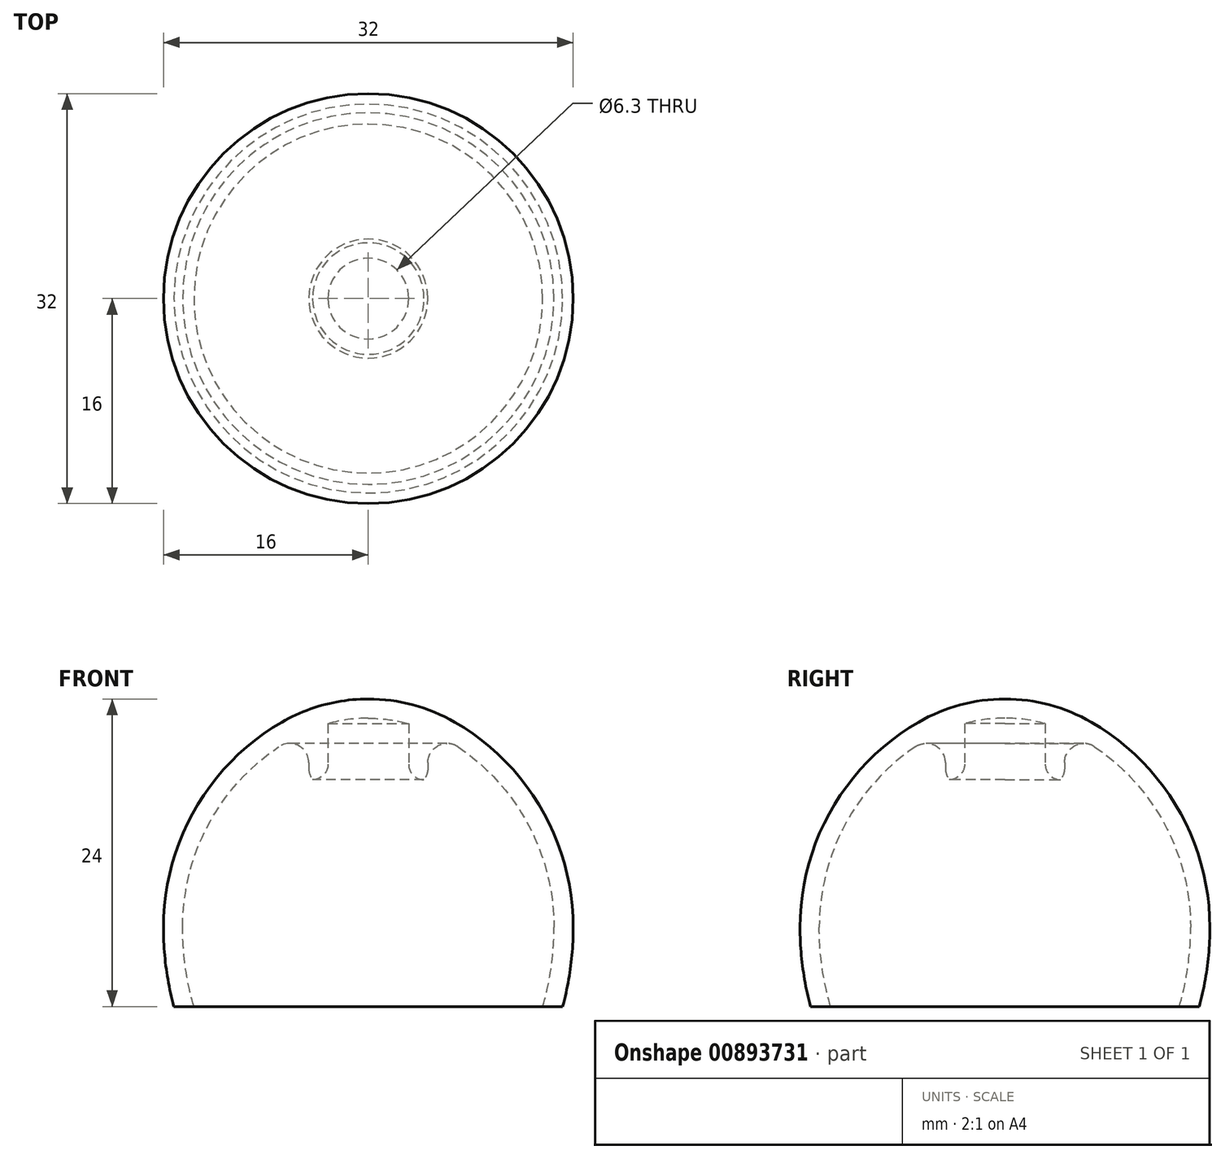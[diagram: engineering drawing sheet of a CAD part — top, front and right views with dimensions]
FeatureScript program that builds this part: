
annotation { "Feature Type Name" : "Feature", "Feature Type Description" : "" }
export const myFeature = defineFeature(function(context is Context, id is Id, definition is map)
    precondition{}
    {
        {
            var Q0;
            Q0=qCreatedBy(makeId("Front.planeOp"),FACE);
            var sketch = newSketch(context, id + "F0", { "sketchPlane" : qUnion([Q0])});
            skLineSegment(sketch, "E0", {"start": v(-4.65, 21.6) * mm, "end": v(-4.65, 17.7) * mm});
            skLineSegment(sketch, "E1", {"start": v(-4.65, 17.7) * mm, "end": v(-3.15, 17.7) * mm});
            skLineSegment(sketch, "E2", {"start": v(-3.15, 17.7) * mm, "end": v(-3.15, 22.2) * mm});
            skLineSegment(sketch, "E3", {"start": v(0, 22.5) * mm, "end": v(0, 24) * mm});
            skArc(sketch, "E4", {"start": v(0, 22.5) * mm, "mid": v(-3.1, 22.1) * mm, "end": v(-6, 20.9) * mm});
            skLineSegment(sketch, "E5", {"start": v(0, 22.5) * mm, "end": v(-16, 22.5) * mm, "construction": true});
            skArc(sketch, "E6", {"start": v(-6, 20.9) * mm, "mid": v(-12.22, 14.67) * mm, "end": v(-14.5, 6.17) * mm});
            skArc(sketch, "E7", {"start": v(-14.5, 6.17) * mm, "mid": v(-14.28, 3.05) * mm, "end": v(-13.62, 0) * mm});
            skArc(sketch, "E8.0", {"start": v(-16, 6.17) * mm, "mid": v(-15.8, 3.06) * mm, "end": v(-15.18, 0) * mm});
            skArc(sketch, "E8.1", {"start": v(-6.75, 22.2) * mm, "mid": v(-13.52, 15.42) * mm, "end": v(-16, 6.17) * mm});
            skArc(sketch, "E8.2", {"start": v(0, 24) * mm, "mid": v(-3.5, 23.54) * mm, "end": v(-6.75, 22.2) * mm});
            skLineSegment(sketch, "E9", {"start": v(-15.18, 0) * mm, "end": v(-13.62, 0) * mm});
            skLineSegment(sketch, "E10", {"start": v(-16, 22.5) * mm, "end": v(-16, 0) * mm, "construction": true});
            skLineSegment(sketch, "E11", {"start": v(-13.62, 0) * mm, "end": v(33.84, 13.87) * mm, "construction": true});
            skLineSegment(sketch, "E12", {"start": v(-14.5, 6.17) * mm, "end": v(32.1, 6.17) * mm, "construction": true});
            skLineSegment(sketch, "E13", {"start": v(-6, 20.9) * mm, "end": v(8.88, -4.88) * mm, "construction": true});
            skSolve(sketch);
        }
        {
            var Q0;
            Q0=qSketchRegion(id+"F0",true);
            var Q1;
            Q1=sQuery(id+"F0.wireOp",EDGE,"E3");
            revolve(context, id + "F1", {"surfaceOperationType" : NewSurfaceOperationType.NEW, "entities" : qUnion([Q0]), "axis" : qUnion([Q1]), "revolveType" : RevolveType.FULL});
        }
        {
            var Q0;
            Q0=makeQuery(id+"F1.opRevolve","SWEPT_EDGE",EDGE,{"disambiguationData":[OSD([sQuery(id+"F0.wireOp",EDGE,"E1"),sQuery(id+"F0.wireOp",EDGE,"E2")])]});
            fillet(context, id + "F2", {"entities" : qUnion([Q0]), "radius" : 1.2 * mm, "tangentPropagation" : true, "allowEdgeOverflow" : false});
        }
        {
            var Q0;
            Q0=makeQuery(id+"F1.opRevolve","SWEPT_EDGE",EDGE,{"disambiguationData":[OSD([sQuery(id+"F0.wireOp",EDGE,"E0"),sQuery(id+"F0.wireOp",EDGE,"E6")])]});
            fillet(context, id + "F3", {"entities" : qUnion([Q0]), "radius" : 1.5 * mm, "tangentPropagation" : true, "allowEdgeOverflow" : false});
        }
    });
